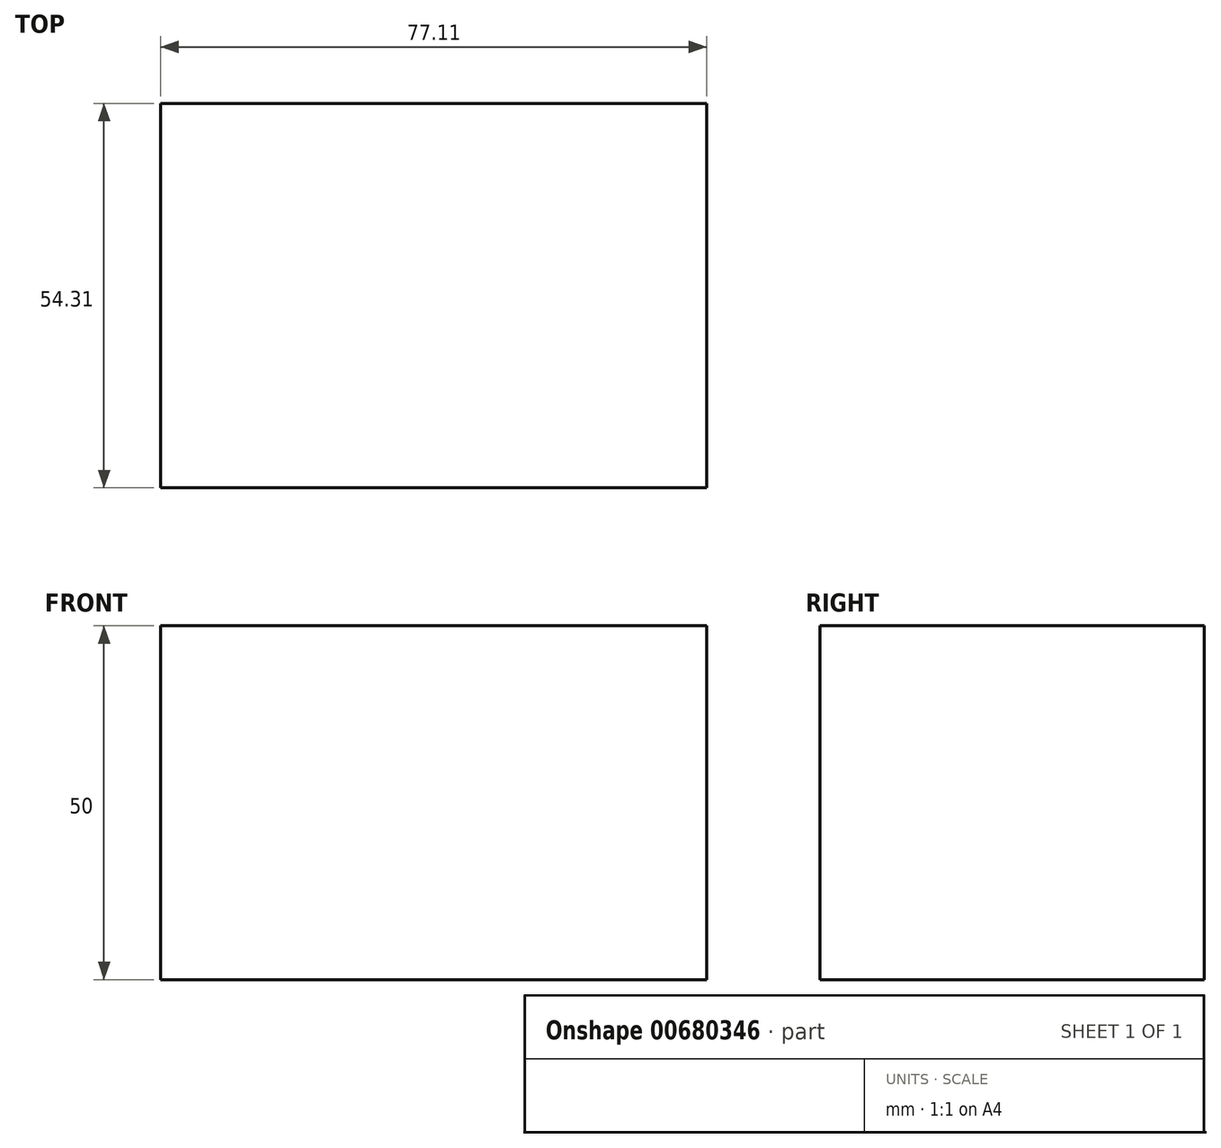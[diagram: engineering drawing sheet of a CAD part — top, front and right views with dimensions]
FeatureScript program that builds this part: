
annotation { "Feature Type Name" : "Feature", "Feature Type Description" : "" }
export const myFeature = defineFeature(function(context is Context, id is Id, definition is map)
    precondition{}
    {
        {
            var Q0;
            Q0=qCreatedBy(makeId("Top.planeOp"),FACE);
            var sketch = newSketch(context, id + "F0", { "sketchPlane" : qUnion([Q0])});
            skLineSegment(sketch, "E0.bottom", {"start": v(-27.57, -19.25) * mm, "end": v(49.54, -19.25) * mm});
            skLineSegment(sketch, "E0.top", {"start": v(-27.57, 35.06) * mm, "end": v(49.54, 35.06) * mm});
            skLineSegment(sketch, "E0.left", {"start": v(-27.57, -19.25) * mm, "end": v(-27.57, 35.06) * mm});
            skLineSegment(sketch, "E0.right", {"start": v(49.54, -19.25) * mm, "end": v(49.54, 35.06) * mm});
            skSolve(sketch);
        }
        {
            var Q0;
            Q0 = qSketchRegion(id + "F0", true);
            extrude(context, id + "F1", {"entities" : qUnion([Q0]), "depth" : 50 * mm, "offsetDistance" : 25 * mm});
        }
    });
